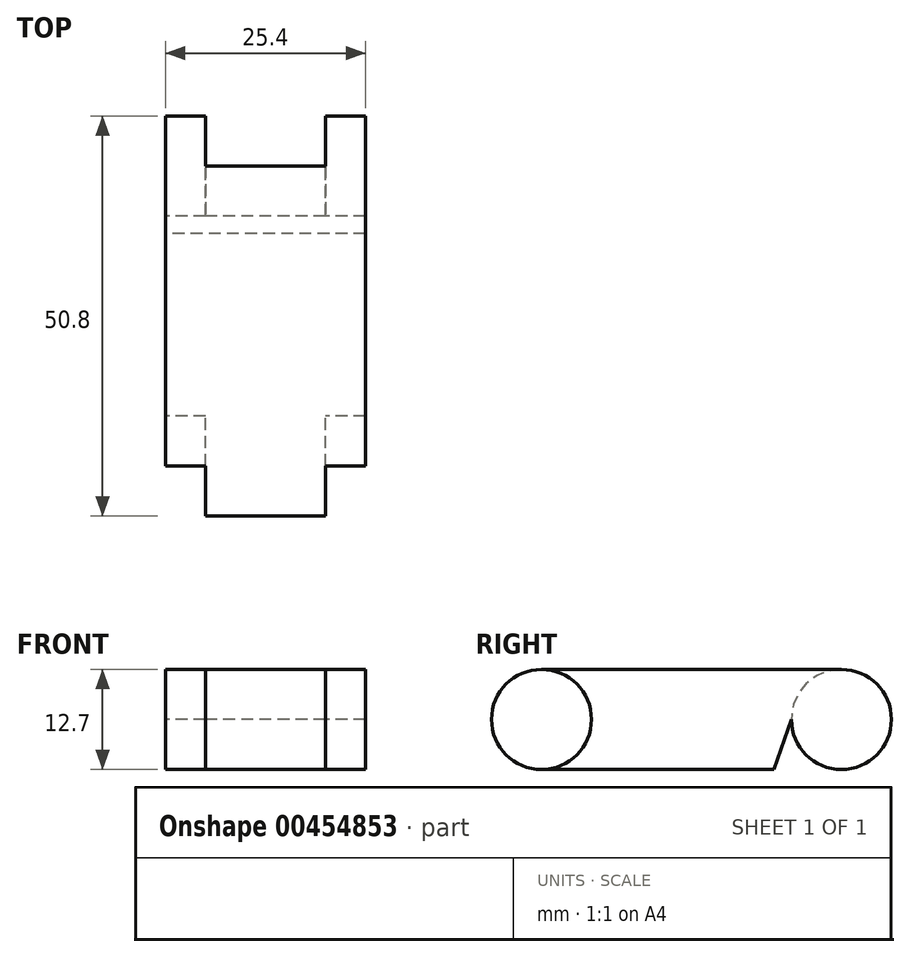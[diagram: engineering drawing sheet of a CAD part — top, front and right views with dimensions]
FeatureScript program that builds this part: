
annotation { "Feature Type Name" : "Feature", "Feature Type Description" : "" }
export const myFeature = defineFeature(function(context is Context, id is Id, definition is map)
    precondition{}
    {
        {
            var Q0;
            Q0=qCreatedBy(makeId("Right.planeOp"),FACE);
            var sketch = newSketch(context, id + "F0", { "sketchPlane" : qUnion([Q0])});
            skLineSegment(sketch, "E0.bottom", {"start": v(19.05, 6.35) * mm, "end": v(-19.05, 6.35) * mm});
            skLineSegment(sketch, "E0.top", {"start": v(10.47, -6.35) * mm, "end": v(-19.05, -6.35) * mm});
            skLineSegment(sketch, "E0.left", {"start": v(19.05, 6.35) * mm, "end": v(19.05, -6.35) * mm});
            skLineSegment(sketch, "E0.right", {"start": v(-19.05, 6.35) * mm, "end": v(-19.05, -6.35) * mm});
            skPoint(sketch, "E0.middle", {"position": v(0, 0) * mm});
            skCircle(sketch, "E1", {"center": v(19.05, 0) * mm, "radius": 6.35 * mm});
            skCircle(sketch, "E2", {"center": v(-19.05, 0) * mm, "radius": 6.35 * mm});
            skLineSegment(sketch, "E3", {"start": v(12.7, 0) * mm, "end": v(10.47, -6.35) * mm});
            skSolve(sketch);
        }
        {
            var Q0;
            {var subQ0=sQuery(id+"F0.wireOp",EDGE,"E0.bottom");Q0=makeQuery(id+"F0.imprint","IMPRINT",FACE,{"disambiguationData":[TD([[makeQuery(id+"F0.imprint","IMPRINT",EDGE,{"derivedFrom":subQ0}),1.0]])]});}
            extrude(context, id + "F1", {"entities" : qUnion([Q0]), "endBound" : BoundingType.SYMMETRIC, "depth" : 25.4 * mm, "offsetDistance" : 25.4 * mm});
        }
        {
            var Q0;
            {var subQ0=sQuery(id+"F0.wireOp",EDGE,"E0.left");Q0=makeQuery(id+"F0.imprint","IMPRINT",FACE,{"disambiguationData":[TD([[makeQuery(id+"F0.imprint","IMPRINT",EDGE,{"derivedFrom":subQ0}),1.0]])]});}
            var Q1;
            {var subQ0=sQuery(id+"F0.wireOp",EDGE,"E0.left");Q1=makeQuery(id+"F0.imprint","IMPRINT",FACE,{"disambiguationData":[TD([[makeQuery(id+"F0.imprint","IMPRINT",EDGE,{"derivedFrom":subQ0}),-1.0]])]});}
            extrude(context, id + "F2", {"entities" : qUnion([Q0, Q1]), "operationType" : NewBodyOperationType.ADD, "depth" : 12.7 * mm, "offsetDistance" : 25.4 * mm, "hasSecondDirection" : true, "secondDirectionOppositeDirection" : false, "secondDirectionDepth" : 7.62 * mm});
        }
        {
            var Q0;
            {var subQ0=sQuery(id+"F0.wireOp",EDGE,"E0.left");Q0=makeQuery(id+"F0.imprint","IMPRINT",FACE,{"disambiguationData":[TD([[makeQuery(id+"F0.imprint","IMPRINT",EDGE,{"derivedFrom":subQ0}),1.0]])]});}
            var Q1;
            {var subQ0=sQuery(id+"F0.wireOp",EDGE,"E0.left");Q1=makeQuery(id+"F0.imprint","IMPRINT",FACE,{"disambiguationData":[TD([[makeQuery(id+"F0.imprint","IMPRINT",EDGE,{"derivedFrom":subQ0}),-1.0]])]});}
            extrude(context, id + "F3", {"entities" : qUnion([Q0, Q1]), "operationType" : NewBodyOperationType.ADD, "oppositeDirection" : true, "depth" : 12.7 * mm, "offsetDistance" : 25.4 * mm, "hasSecondDirection" : true, "secondDirectionOppositeDirection" : true, "secondDirectionDepth" : 7.62 * mm});
        }
        {
            var Q0;
            {var subQ0=sQuery(id+"F0.wireOp",EDGE,"E0.right");Q0=makeQuery(id+"F0.imprint","IMPRINT",FACE,{"disambiguationData":[TD([[makeQuery(id+"F0.imprint","IMPRINT",EDGE,{"derivedFrom":subQ0}),1.0]])]});}
            var Q1;
            {var subQ0=sQuery(id+"F0.wireOp",EDGE,"E0.right");Q1=makeQuery(id+"F0.imprint","IMPRINT",FACE,{"disambiguationData":[TD([[makeQuery(id+"F0.imprint","IMPRINT",EDGE,{"derivedFrom":subQ0}),-1.0]])]});}
            extrude(context, id + "F4", {"entities" : qUnion([Q0, Q1]), "operationType" : NewBodyOperationType.ADD, "endBound" : BoundingType.SYMMETRIC, "depth" : 15.24 * mm, "offsetDistance" : 25.4 * mm});
        }
    });
